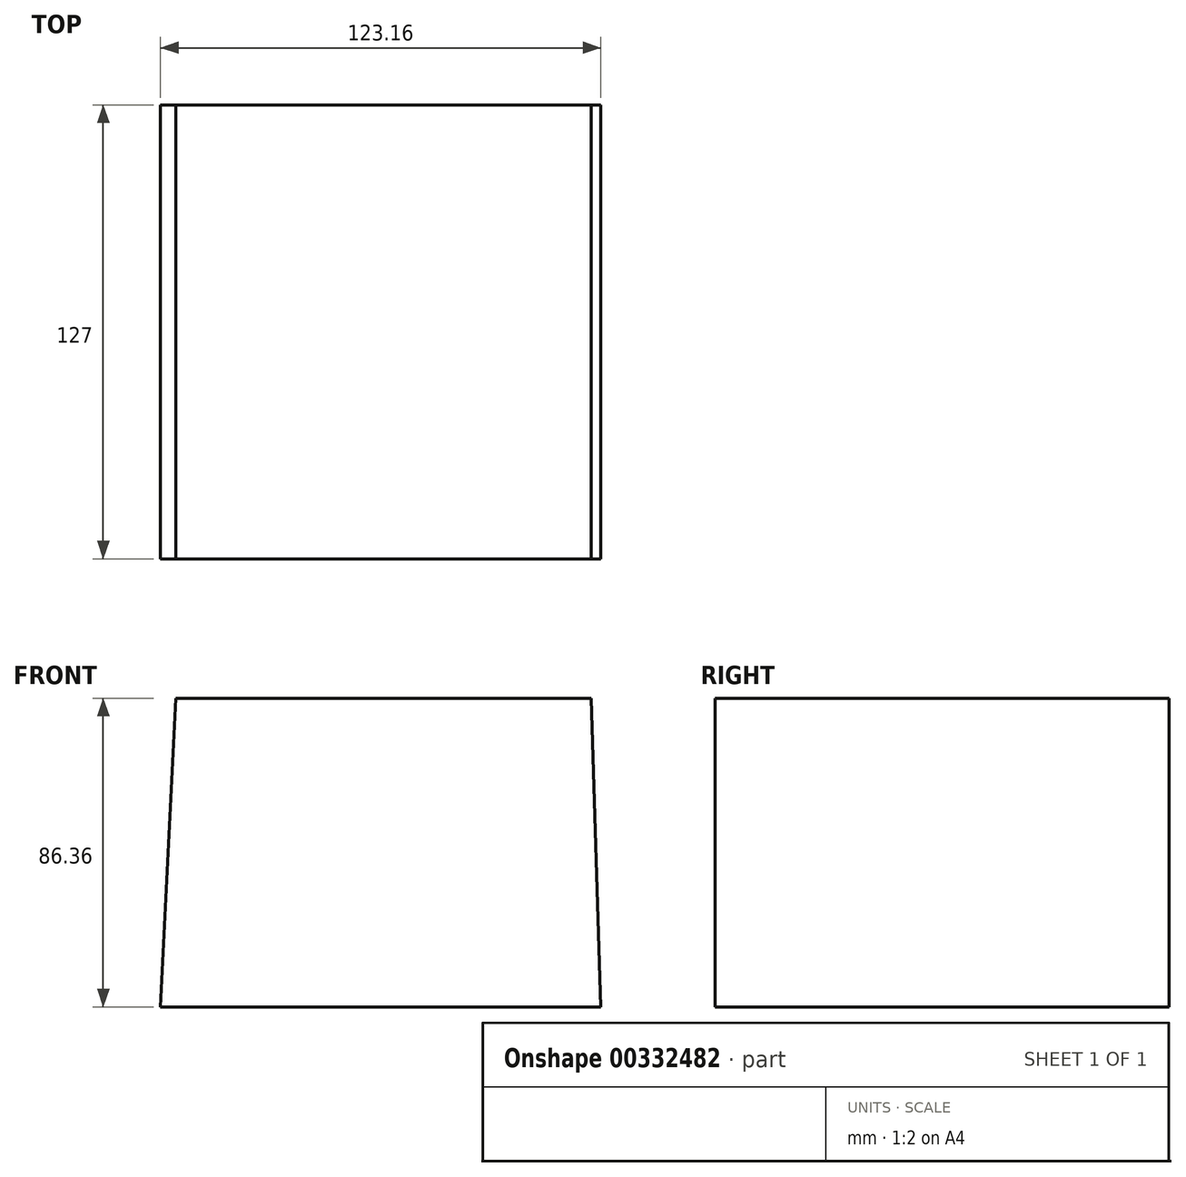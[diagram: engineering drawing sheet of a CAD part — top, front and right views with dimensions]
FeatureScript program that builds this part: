
annotation { "Feature Type Name" : "Feature", "Feature Type Description" : "" }
export const myFeature = defineFeature(function(context is Context, id is Id, definition is map)
    precondition{}
    {
        {
            var Q0;
            Q0=qCreatedBy(makeId("Front.planeOp"),FACE);
            var sketch = newSketch(context, id + "F0", { "sketchPlane" : qUnion([Q0])});
            skLineSegment(sketch, "E0", {"start": v(-60.74, 49.76) * mm, "end": v(55.45, 49.76) * mm});
            skLineSegment(sketch, "E1", {"start": v(55.45, 49.76) * mm, "end": v(58.16, -36.6) * mm});
            skLineSegment(sketch, "E2", {"start": v(58.16, -36.6) * mm, "end": v(-65, -36.6) * mm});
            skLineSegment(sketch, "E3", {"start": v(-65, -36.6) * mm, "end": v(-60.74, 49.76) * mm});
            skLineSegment(sketch, "E4", {"start": v(-60.74, 49.76) * mm, "end": v(58.16, -36.6) * mm});
            skSolve(sketch);
        }
        {
            var Q0;
            Q0=sQuery(id+"F0.wireOp",EDGE,"E1");
            var Q1;
            Q1=sQuery(id+"F0.wireOp",EDGE,"E2");
            var Q2;
            Q2=sQuery(id+"F0.wireOp",EDGE,"E3");
            var Q3;
            Q3=sQuery(id+"F0.wireOp",EDGE,"E0");
            extrude(context, id + "F1", {"bodyType" : ToolBodyType.SURFACE, "surfaceEntities" : qUnion([Q0, Q1, Q2, Q3]), "depth" : 127 * mm});
        }
    });
